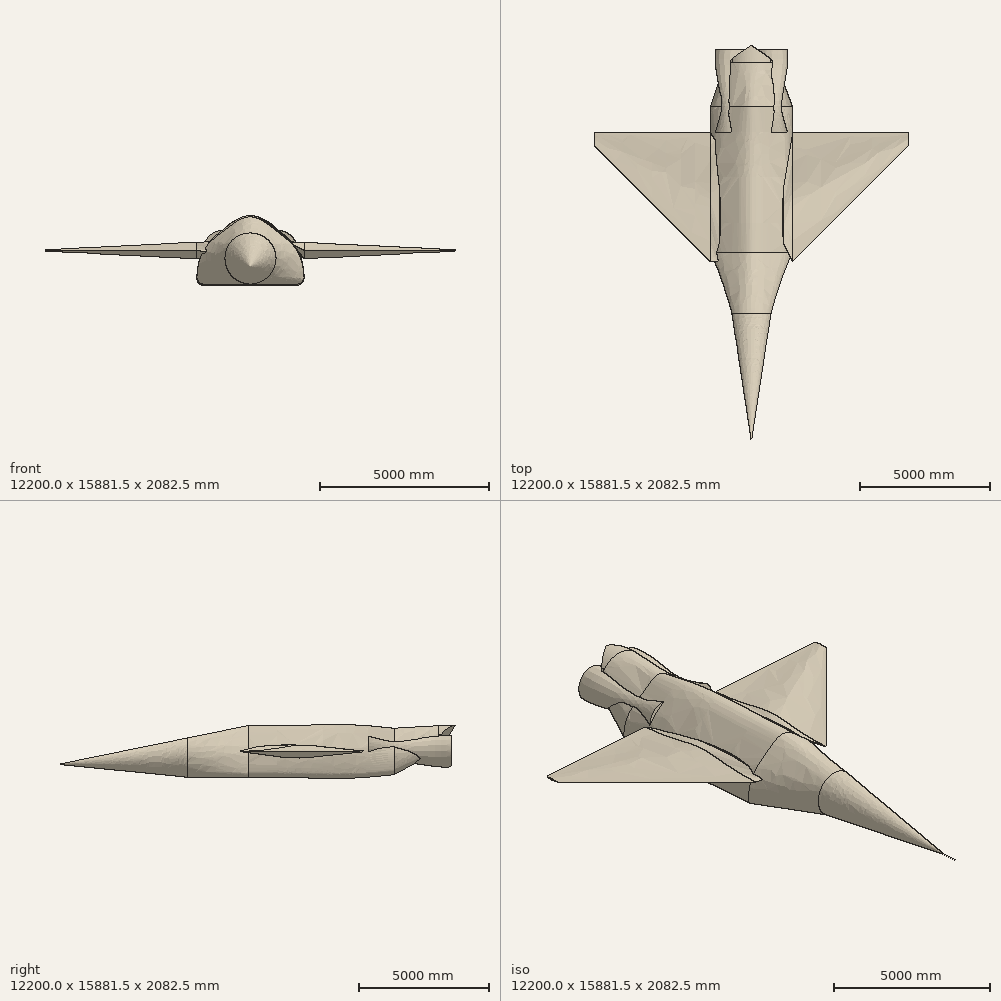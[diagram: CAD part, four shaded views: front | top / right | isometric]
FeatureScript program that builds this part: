
annotation { "Feature Type Name" : "Feature", "Feature Type Description" : "" }
export const myFeature = defineFeature(function(context is Context, id is Id, definition is map)
    precondition{}
    {
        {
            var Q0;
            Q0=qCreatedBy(makeId("Right.planeOp"),FACE);
            var sketch = newSketch(context, id + "F0", { "sketchPlane" : qUnion([Q0])});
            skLineSegment(sketch, "E0", {"start": v(0, 0) * mm, "end": v(-1750, 0) * mm});
            skLineSegment(sketch, "E1", {"start": v(-1750, 0) * mm, "end": v(-3500, 0) * mm});
            skLineSegment(sketch, "E2", {"start": v(-3500, 0) * mm, "end": v(-3500, -1000) * mm});
            skLineSegment(sketch, "E3", {"start": v(-3500, -1000) * mm, "end": v(-8500, -1000) * mm});
            skLineSegment(sketch, "E4", {"start": v(-8500, -1000) * mm, "end": v(-8500, -499.31) * mm});
            skLineSegment(sketch, "E5", {"start": v(-1151.4, 0) * mm, "end": v(-1151.4, 1000) * mm});
            skLineSegment(sketch, "E6", {"start": v(-1151.4, 1000) * mm, "end": v(-8500, -499.31) * mm});
            skLineSegment(sketch, "E7", {"start": v(-8500, -499.31) * mm, "end": v(-3500, -1000) * mm});
            skLineSegment(sketch, "E8", {"start": v(-3500, 0) * mm, "end": v(-3500, 520.82) * mm});
            skLineSegment(sketch, "E9", {"start": v(-8500, -499.31) * mm, "end": v(-8450, -499.31) * mm});
            skLineSegment(sketch, "E10", {"start": v(-8450, -499.31) * mm, "end": v(-8450, -489.1) * mm});
            skLineSegment(sketch, "E11", {"start": v(-8450, -499.31) * mm, "end": v(-8450, -504.32) * mm});
            skSolve(sketch);
        }
        {
            var Q0;
            Q0=sQuery(id+"F0.wireOp",EDGE,"E5");
            cPlane(context, id + "F1", {"entities" : qUnion([Q0]), "cplaneType" : CPlaneType.LINE_ANGLE, "offset" : 25 * mm, "angle" : 90 * degree, "oppositeDirection" : true, "width" : 150 * mm, "height" : 150 * mm});
        }
        {
            var Q0;
            Q0=qCreatedBy(id+"F1.planeOp",FACE);
            var sketch = newSketch(context, id + "F2", { "sketchPlane" : qUnion([Q0])});
            skLineSegment(sketch, "E12.top", {"start": v(-1394.2, -1000) * mm, "end": v(1394.2, -1000) * mm});
            skPoint(sketch, "E12.middle", {"position": v(0, 0) * mm});
            skFitSpline(sketch, "E13", {"points": [v(-1600, -1000) * mm, v(-848, 530) * mm, v(0, 1000) * mm, v(848, 530) * mm, v(1600, -1000) * mm], "startDerivative": vector(0, 10524.75) * mm, "endDerivative": vector(0, -10524.75) * mm});
            skArc(sketch, "E14", {"start": v(-735.27, 618.52) * mm, "mid": v(-1273.27, 435.52) * mm, "end": v(-1440.68, -107.53) * mm});
            skArc(sketch, "E15", {"start": v(1440.68, -107.53) * mm, "mid": v(1273.27, 435.52) * mm, "end": v(735.27, 618.52) * mm});
            skFitSpline(sketch, "E16.trimOffspring", {"points": [v(-1600, -1000) * mm, v(-848, 530) * mm, v(0, 1000) * mm, v(848, 530) * mm, v(1600, -1000) * mm], "startDerivative": vector(0, 10524.75) * mm, "endDerivative": vector(0, -10524.75) * mm});
            skFitSpline(sketch, "E17.trimOffspring", {"points": [v(-1600, -1000) * mm, v(-848, 530) * mm, v(0, 1000) * mm, v(848, 530) * mm, v(1600, -1000) * mm], "startDerivative": vector(0, 10524.75) * mm, "endDerivative": vector(0, -10524.75) * mm});
            skArc(sketch, "E18.filletArc", {"start": v(-1593.82, -787.83) * mm, "mid": v(-1539.85, -937.05) * mm, "end": v(-1394.2, -1000) * mm});
            skArc(sketch, "E19.filletArc", {"start": v(1394.2, -1000) * mm, "mid": v(1539.85, -937.05) * mm, "end": v(1593.82, -787.83) * mm});
            skSolve(sketch);
        }
        {
            var Q0;
            Q0=qCreatedBy(makeId("Front.planeOp"),FACE);
            var sketch = newSketch(context, id + "F3", { "sketchPlane" : qUnion([Q0])});
            skLineSegment(sketch, "E20.top", {"start": v(-1394.2, -1000) * mm, "end": v(1394.2, -1000) * mm});
            skPoint(sketch, "E20.middle", {"position": v(0, 0) * mm});
            skFitSpline(sketch, "E21", {"points": [v(-1600, -1000) * mm, v(-848, 530) * mm, v(0, 1000) * mm, v(848, 530) * mm, v(1600, -1000) * mm], "startDerivative": vector(0, 10524.75) * mm, "endDerivative": vector(0, -10524.75) * mm});
            skArc(sketch, "E22", {"start": v(-735.27, 618.52) * mm, "mid": v(-1273.27, 435.52) * mm, "end": v(-1440.68, -107.53) * mm});
            skArc(sketch, "E23", {"start": v(1440.68, -107.53) * mm, "mid": v(1273.27, 435.52) * mm, "end": v(735.27, 618.52) * mm});
            skFitSpline(sketch, "E24.trimOffspring", {"points": [v(-1600, -1000) * mm, v(-848, 530) * mm, v(0, 1000) * mm, v(848, 530) * mm, v(1600, -1000) * mm], "startDerivative": vector(0, 10524.75) * mm, "endDerivative": vector(0, -10524.75) * mm});
            skFitSpline(sketch, "E25.trimOffspring", {"points": [v(-1600, -1000) * mm, v(-848, 530) * mm, v(0, 1000) * mm, v(848, 530) * mm, v(1600, -1000) * mm], "startDerivative": vector(0, 10524.75) * mm, "endDerivative": vector(0, -10524.75) * mm});
            skArc(sketch, "E26.filletArc", {"start": v(-1593.82, -787.83) * mm, "mid": v(-1539.85, -937.05) * mm, "end": v(-1394.2, -1000) * mm});
            skArc(sketch, "E27.filletArc", {"start": v(1394.2, -1000) * mm, "mid": v(1539.85, -937.05) * mm, "end": v(1593.82, -787.83) * mm});
            skSolve(sketch);
        }
        {
            var Q0;
            Q0=qCreatedBy(makeId("Front.planeOp"),FACE);
            cPlane(context, id + "F4", {"entities" : qUnion([Q0]), "cplaneType" : CPlaneType.OFFSET, "offset" : 3500 * mm, "oppositeDirection" : true, "width" : 150 * mm, "height" : 150 * mm});
        }
        {
            var Q0;
            Q0=qCreatedBy(id+"F4.planeOp",FACE);
            var sketch = newSketch(context, id + "F5", { "sketchPlane" : qUnion([Q0])});
            skLineSegment(sketch, "E28.top", {"start": v(-1394.2, -1000) * mm, "end": v(1394.2, -1000) * mm});
            skPoint(sketch, "E28.middle", {"position": v(0, 0) * mm});
            skFitSpline(sketch, "E29", {"points": [v(-1600, -1000) * mm, v(-848, 530) * mm, v(0, 1000) * mm, v(848, 530) * mm, v(1600, -1000) * mm], "startDerivative": vector(0, 10524.75) * mm, "endDerivative": vector(0, -10524.75) * mm});
            skArc(sketch, "E30", {"start": v(-735.27, 618.52) * mm, "mid": v(-1273.27, 435.52) * mm, "end": v(-1440.68, -107.53) * mm});
            skArc(sketch, "E31", {"start": v(1440.68, -107.53) * mm, "mid": v(1273.27, 435.52) * mm, "end": v(735.27, 618.52) * mm});
            skFitSpline(sketch, "E32.trimOffspring", {"points": [v(-1600, -1000) * mm, v(-848, 530) * mm, v(0, 1000) * mm, v(848, 530) * mm, v(1600, -1000) * mm], "startDerivative": vector(0, 10524.75) * mm, "endDerivative": vector(0, -10524.75) * mm});
            skFitSpline(sketch, "E33.trimOffspring", {"points": [v(-1600, -1000) * mm, v(-848, 530) * mm, v(0, 1000) * mm, v(848, 530) * mm, v(1600, -1000) * mm], "startDerivative": vector(0, 10524.75) * mm, "endDerivative": vector(0, -10524.75) * mm});
            skArc(sketch, "E34.filletArc", {"start": v(-1593.82, -787.83) * mm, "mid": v(-1539.85, -937.05) * mm, "end": v(-1394.2, -1000) * mm});
            skArc(sketch, "E35.filletArc", {"start": v(1394.2, -1000) * mm, "mid": v(1539.85, -937.05) * mm, "end": v(1593.82, -787.83) * mm});
            skSolve(sketch);
        }
        {
            var Q0;
            Q0=qCreatedBy(makeId("Front.planeOp"),FACE);
            cPlane(context, id + "F6", {"entities" : qUnion([Q0]), "cplaneType" : CPlaneType.OFFSET, "offset" : 4500 * mm, "oppositeDirection" : true, "width" : 150 * mm, "height" : 150 * mm});
        }
        {
            var Q0;
            Q0=qCreatedBy(id+"F6.planeOp",FACE);
            var sketch = newSketch(context, id + "F7", { "sketchPlane" : qUnion([Q0])});
            skLineSegment(sketch, "E36.top", {"start": v(-1413.07, -900) * mm, "end": v(1413.07, -900) * mm});
            skPoint(sketch, "E36.middle", {"position": v(0, 0) * mm});
            skFitSpline(sketch, "E37", {"points": [v(-1600, -900) * mm, v(-784.42, 441.24) * mm, v(0, 900) * mm, v(784.42, 441.24) * mm, v(1600, -900) * mm], "startDerivative": vector(0, 9508.62) * mm, "endDerivative": vector(0, -9508.62) * mm});
            skArc(sketch, "E38", {"start": v(-719.25, 488.69) * mm, "mid": v(-1131.76, 394.84) * mm, "end": v(-1324.66, 18.33) * mm});
            skArc(sketch, "E39", {"start": v(1324.66, 18.33) * mm, "mid": v(1131.76, 394.84) * mm, "end": v(719.25, 488.69) * mm});
            skFitSpline(sketch, "E40.trimOffspring", {"points": [v(-1600, -900) * mm, v(-784.42, 441.24) * mm, v(0, 900) * mm, v(784.42, 441.24) * mm, v(1600, -900) * mm], "startDerivative": vector(0, 9508.62) * mm, "endDerivative": vector(0, -9508.62) * mm});
            skFitSpline(sketch, "E41.trimOffspring", {"points": [v(-1600, -900) * mm, v(-784.42, 441.24) * mm, v(0, 900) * mm, v(784.42, 441.24) * mm, v(1600, -900) * mm], "startDerivative": vector(0, 9508.62) * mm, "endDerivative": vector(0, -9508.62) * mm});
            skArc(sketch, "E42.filletArc", {"start": v(-1592.48, -705.43) * mm, "mid": v(-1545.4, -842.02) * mm, "end": v(-1413.07, -900) * mm});
            skArc(sketch, "E43.filletArc", {"start": v(1413.07, -900) * mm, "mid": v(1545.4, -842.02) * mm, "end": v(1592.48, -705.43) * mm});
            skLineSegment(sketch, "E44", {"start": v(-719.25, 488.69) * mm, "end": v(-1324.66, 18.33) * mm, "construction": true});
            skLineSegment(sketch, "E45", {"start": v(719.25, 488.69) * mm, "end": v(1324.66, 18.33) * mm, "construction": true});
            skSolve(sketch);
        }
        {
            var Q0;
            Q0=qCreatedBy(makeId("Front.planeOp"),FACE);
            cPlane(context, id + "F8", {"entities" : qUnion([Q0]), "cplaneType" : CPlaneType.OFFSET, "offset" : 6232.05 * mm, "oppositeDirection" : true, "width" : 150 * mm, "height" : 150 * mm});
        }
        {
            var Q0;
            Q0=qCreatedBy(id+"F8.planeOp",FACE);
            var sketch = newSketch(context, id + "F9", { "sketchPlane" : qUnion([Q0])});
            skArc(sketch, "E46", {"start": v(998.61, 52.63) * mm, "mid": v(0, 1000) * mm, "end": v(-998.61, 52.63) * mm});
            skLineSegment(sketch, "E47", {"start": v(0, 0) * mm, "end": v(-948.68, 0) * mm});
            skLineSegment(sketch, "E48", {"start": v(0, 0) * mm, "end": v(948.68, 0) * mm});
            skLineSegment(sketch, "E49", {"start": v(0, 1000) * mm, "end": v(0, 675) * mm, "construction": true});
            skLineSegment(sketch, "E50", {"start": v(0, 675) * mm, "end": v(-737.82, 675) * mm, "construction": true});
            skLineSegment(sketch, "E51", {"start": v(0, 675) * mm, "end": v(737.82, 675) * mm, "construction": true});
            skPoint(sketch, "E52.visualSharp", {"position": v(-1000, 0) * mm});
            skArc(sketch, "E52.filletArc", {"start": v(-998.61, 52.63) * mm, "mid": v(-984.96, 15.59) * mm, "end": v(-948.68, 0) * mm});
            skPoint(sketch, "E53.visualSharp", {"position": v(1000, 0) * mm});
            skArc(sketch, "E53.filletArc", {"start": v(948.68, 0) * mm, "mid": v(984.96, 15.59) * mm, "end": v(998.61, 52.63) * mm});
            skSolve(sketch);
        }
        {
            var Q0;
            Q0=makeQuery(id+"F2.imprint","IMPRINT",FACE,{"disambiguationData":[TD([[makeQuery(id+"F2.imprint","IMPRINT",EDGE,{"derivedFrom":sQuery(id+"F2.wireOp",EDGE,"E12.top")}),1.0]])]});
            var Q1;
            Q1=makeQuery(id+"F3.imprint","IMPRINT",FACE,{"disambiguationData":[TD([[makeQuery(id+"F3.imprint","IMPRINT",EDGE,{"derivedFrom":sQuery(id+"F3.wireOp",EDGE,"E20.top")}),1.0]])]});
            var Q2;
            Q2=makeQuery(id+"F5.imprint","IMPRINT",FACE,{"disambiguationData":[TD([[makeQuery(id+"F5.imprint","IMPRINT",EDGE,{"derivedFrom":sQuery(id+"F5.wireOp",EDGE,"E28.top")}),1.0]])]});
            var Q3;
            Q3=makeQuery(id+"F7.imprint","IMPRINT",FACE,{"disambiguationData":[TD([[makeQuery(id+"F7.imprint","IMPRINT",EDGE,{"derivedFrom":sQuery(id+"F7.wireOp",EDGE,"E36.top")}),1.0]])]});
            loft(context, id + "F10", {"sheetProfilesArray" : [{ "sheetProfileEntities" : qUnion([Q0]) }, { "sheetProfileEntities" : qUnion([Q1]) }, { "sheetProfileEntities" : qUnion([Q2]) }, { "sheetProfileEntities" : qUnion([Q3]) }]});
        }
        {
            var Q0;
            Q0=sQuery(id+"F7.wireOp",EDGE,"E44");
            var Q1;
            Q1=sQuery(id+"F9.wireOp",VERTEX,"E50.end");
            cPlane(context, id + "F11", {"entities" : qUnion([Q0, Q1]), "cplaneType" : CPlaneType.LINE_ANGLE, "offset" : 25 * mm, "angle" : 180 * degree, "width" : 150 * mm, "height" : 150 * mm});
        }
        {
            var Q0;
            Q0=qCreatedBy(id+"F11.planeOp",FACE);
            var sketch = newSketch(context, id + "F12", { "sketchPlane" : qUnion([Q0])});
            skLineSegment(sketch, "E54", {"start": v(-589.34, 4526.34) * mm, "end": v(-612.8, 6268.32) * mm});
            skLineSegment(sketch, "E55", {"start": v(-1354.08, 4472.19) * mm, "end": v(-612.8, 6268.32) * mm});
            skSolve(sketch);
        }
        {
            var Q0;
            Q0=sQuery(id+"F7.wireOp",EDGE,"E45");
            var Q1;
            Q1=sQuery(id+"F9.wireOp",VERTEX,"E51.end");
            cPlane(context, id + "F13", {"entities" : qUnion([Q0, Q1]), "cplaneType" : CPlaneType.LINE_ANGLE, "offset" : 25 * mm, "angle" : 0 * degree, "width" : 150 * mm, "height" : 150 * mm});
        }
        {
            var Q0;
            Q0=qCreatedBy(id+"F13.planeOp",FACE);
            var sketch = newSketch(context, id + "F14", { "sketchPlane" : qUnion([Q0])});
            skLineSegment(sketch, "E56", {"start": v(589.34, 4526.34) * mm, "end": v(612.8, 6268.32) * mm});
            skLineSegment(sketch, "E57", {"start": v(1354.08, 4472.19) * mm, "end": v(612.8, 6268.32) * mm});
            skSolve(sketch);
        }
        {
            var Q1;
            Q1=makeQuery(id+"F10.opLoft","CAP_FACE",FACE,{"disambiguationData":[OSD([makeQuery(id+"F7.imprint","IMPRINT",FACE,{"disambiguationData":[TD([[makeQuery(id+"F7.imprint","IMPRINT",EDGE,{"derivedFrom":sQuery(id+"F7.wireOp",EDGE,"E36.top")}),1.0]])]})])],"isStart":true});
            var Q2;
            Q2=makeQuery(id+"F9.imprint","IMPRINT",FACE,{"disambiguationData":[TD([[makeQuery(id+"F9.imprint","IMPRINT",EDGE,{"derivedFrom":sQuery(id+"F9.wireOp",EDGE,"E46")}),1.0]])]});
            var Q3;
            Q3=sQuery(id+"F12.wireOp",EDGE,"E54");
            var Q4;
            Q4=sQuery(id+"F14.wireOp",EDGE,"E56");
            loft(context, id + "F15", {"operationType" : NewBodyOperationType.ADD, "addGuides" : true, "sheetProfilesArray" : [{ "sheetProfileEntities" : qUnion([Q1]) }, { "sheetProfileEntities" : qUnion([Q2]) }], "guidesArray" : [{ "guideEntities" : qUnion([Q3]), "guideDerivativeType" : LoftGuideDerivativeType.DEFAULT, "guideDerivativeMagnitude" : 1 }, { "guideEntities" : qUnion([Q4]), "guideDerivativeType" : LoftGuideDerivativeType.DEFAULT, "guideDerivativeMagnitude" : 1 }]});
        }
        {
            var Q0;
            Q0=makeQuery(id+"F15.opLoft","CAP_FACE",FACE,{"disambiguationData":[OSD([makeQuery(id+"F9.imprint","IMPRINT",FACE,{"disambiguationData":[TD([[makeQuery(id+"F9.imprint","IMPRINT",EDGE,{"derivedFrom":sQuery(id+"F9.wireOp",EDGE,"E46")}),1.0]])]})])],"isStart":true});
            extrude(context, id + "F16", {"entities" : qUnion([Q0]), "operationType" : NewBodyOperationType.ADD, "depth" : 649.4 * mm, "offsetDistance" : 25 * mm});
        }
        {
            var Q0;
            Q0=qCreatedBy(makeId("Right.planeOp"),FACE);
            var sketch = newSketch(context, id + "F17", { "sketchPlane" : qUnion([Q0])});
            skLineSegment(sketch, "E58", {"start": v(0, 0) * mm, "end": v(4500, 0) * mm});
            skLineSegment(sketch, "E59", {"start": v(4500, 0) * mm, "end": v(6232.05, 0) * mm});
            skLineSegment(sketch, "E60", {"start": v(4500, 0) * mm, "end": v(4500, 1000) * mm});
            skLineSegment(sketch, "E61", {"start": v(4500, 1000) * mm, "end": v(6881.46, 1000) * mm});
            skLineSegment(sketch, "E62", {"start": v(6881.46, 1000) * mm, "end": v(6881.46, -1000) * mm});
            skLineSegment(sketch, "E63", {"start": v(6881.46, 1000) * mm, "end": v(6232.05, 0) * mm});
            skLineSegment(sketch, "E64", {"start": v(6232.05, 0) * mm, "end": v(5582.64, -1000) * mm});
            skLineSegment(sketch, "E65", {"start": v(5582.64, -1000) * mm, "end": v(6881.46, -1000) * mm});
            skSolve(sketch);
        }
        {
            var Q0;
            Q0=makeQuery(id+"F17.imprint","IMPRINT",FACE,{"disambiguationData":[TD([[makeQuery(id+"F17.imprint","IMPRINT",EDGE,{"derivedFrom":sQuery(id+"F17.wireOp",EDGE,"E62")}),-1.0]])]});
            var Q1;
            Q1=sQuery(id+"F17.wireOp",EDGE,"E61");
            revolve(context, id + "F18", {"operationType" : NewBodyOperationType.REMOVE, "entities" : qUnion([Q0]), "axis" : qUnion([Q1]), "revolveType" : RevolveType.SYMMETRIC, "oppositeDirection" : true, "angle" : 182 * degree});
        }
        {
            var Q0;
            Q0=qCreatedBy(id+"F1.planeOp",FACE);
            var sketch = newSketch(context, id + "F19", { "sketchPlane" : qUnion([Q0])});
            skLineSegment(sketch, "E66.top", {"start": v(-1394.2, -1000) * mm, "end": v(1394.2, -1000) * mm});
            skPoint(sketch, "E66.middle", {"position": v(0, 0) * mm});
            skFitSpline(sketch, "E67", {"points": [v(-1600, -1000) * mm, v(-848, 530) * mm, v(0, 1000) * mm, v(848, 530) * mm, v(1600, -1000) * mm], "startDerivative": vector(0, 10524.75) * mm, "endDerivative": vector(0, -10524.75) * mm});
            skArc(sketch, "E68.filletArc", {"start": v(-1593.82, -787.83) * mm, "mid": v(-1539.85, -937.05) * mm, "end": v(-1394.2, -1000) * mm});
            skArc(sketch, "E69.filletArc", {"start": v(1394.2, -1000) * mm, "mid": v(1539.85, -937.05) * mm, "end": v(1593.82, -787.83) * mm});
            skLineSegment(sketch, "E70", {"start": v(-1593.82, -787.83) * mm, "end": v(-1394.2, -1000) * mm, "construction": true});
            skLineSegment(sketch, "E71", {"start": v(1593.82, -787.83) * mm, "end": v(1394.2, -1000) * mm, "construction": true});
            skSolve(sketch);
        }
        {
            var Q0;
            Q0=qCreatedBy(makeId("Front.planeOp"),FACE);
            cPlane(context, id + "F20", {"entities" : qUnion([Q0]), "cplaneType" : CPlaneType.OFFSET, "offset" : 3500 * mm, "width" : 150 * mm, "height" : 150 * mm});
        }
        {
            var Q0;
            Q0=qCreatedBy(id+"F20.planeOp",FACE);
            var sketch = newSketch(context, id + "F21", { "sketchPlane" : qUnion([Q0])});
            skCircle(sketch, "E72", {"center": v(0, -239.59) * mm, "radius": 760.41 * mm});
            skLineSegment(sketch, "E73", {"start": v(0, -1000) * mm, "end": v(0, -800) * mm, "construction": true});
            skLineSegment(sketch, "E74", {"start": v(0, -800) * mm, "end": v(-513.97, -800) * mm, "construction": true});
            skLineSegment(sketch, "E75", {"start": v(0, -800) * mm, "end": v(513.97, -800) * mm, "construction": true});
            skSolve(sketch);
        }
        {
            var Q0;
            Q0=qCreatedBy(makeId("Front.planeOp"),FACE);
            cPlane(context, id + "F22", {"entities" : qUnion([Q0]), "cplaneType" : CPlaneType.OFFSET, "offset" : 8450 * mm, "width" : 150 * mm, "height" : 150 * mm});
        }
        {
            var Q0;
            Q0=qCreatedBy(id+"F22.planeOp",FACE);
            var sketch = newSketch(context, id + "F23", { "sketchPlane" : qUnion([Q0])});
            skCircle(sketch, "E76", {"center": v(0, -496.71) * mm, "radius": 7.6 * mm});
            skSolve(sketch);
        }
        {
            var Q0;
            Q0=sQuery(id+"F19.wireOp",EDGE,"E70");
            var Q1;
            Q1=sQuery(id+"F21.wireOp",VERTEX,"E74.end");
            cPlane(context, id + "F24", {"entities" : qUnion([Q0, Q1]), "cplaneType" : CPlaneType.LINE_ANGLE, "offset" : 25 * mm, "angle" : 0 * degree, "width" : 150 * mm, "height" : 150 * mm});
        }
        {
            var Q0;
            Q0=qCreatedBy(id+"F24.planeOp",FACE);
            var sketch = newSketch(context, id + "F25", { "sketchPlane" : qUnion([Q0])});
            skLineSegment(sketch, "E77", {"start": v(3032.27, -230.44) * mm, "end": v(558.11, 518.4) * mm});
            skLineSegment(sketch, "E78", {"start": v(3032.27, -230.44) * mm, "end": v(558.11, 227.09) * mm});
            skSolve(sketch);
        }
        {
            var Q0;
            Q0=sQuery(id+"F19.wireOp",EDGE,"E71");
            var Q1;
            Q1=sQuery(id+"F21.wireOp",VERTEX,"E75.end");
            cPlane(context, id + "F26", {"entities" : qUnion([Q0, Q1]), "cplaneType" : CPlaneType.LINE_ANGLE, "offset" : 25 * mm, "angle" : 180 * degree, "width" : 150 * mm, "height" : 150 * mm});
        }
        {
            var Q0;
            Q0=qCreatedBy(id+"F26.planeOp",FACE);
            var sketch = newSketch(context, id + "F27", { "sketchPlane" : qUnion([Q0])});
            skLineSegment(sketch, "E79", {"start": v(-3032.27, -230.44) * mm, "end": v(-558.11, 518.4) * mm});
            skLineSegment(sketch, "E80", {"start": v(-3032.27, -230.44) * mm, "end": v(-558.11, 227.09) * mm});
            skSolve(sketch);
        }
        {
            var Q1;
            Q1=makeQuery(id+"F19.imprint","IMPRINT",FACE,{"disambiguationData":[TD([[makeQuery(id+"F19.imprint","IMPRINT",EDGE,{"derivedFrom":sQuery(id+"F19.wireOp",EDGE,"E66.top")}),1.0]])]});
            var Q2;
            Q2=makeQuery(id+"F21.imprint","IMPRINT",FACE,{"disambiguationData":[TD([[makeQuery(id+"F21.imprint","IMPRINT",EDGE,{"derivedFrom":sQuery(id+"F21.wireOp",EDGE,"E72")}),1.0]])]});
            var Q3;
            Q3=sQuery(id+"F25.wireOp",EDGE,"E77");
            var Q4;
            Q4=sQuery(id+"F27.wireOp",EDGE,"E79");
            loft(context, id + "F28", {"operationType" : NewBodyOperationType.ADD, "addGuides" : true, "sheetProfilesArray" : [{ "sheetProfileEntities" : qUnion([Q1]) }, { "sheetProfileEntities" : qUnion([Q2]) }], "guidesArray" : [{ "guideEntities" : qUnion([Q3]), "guideDerivativeType" : LoftGuideDerivativeType.DEFAULT, "guideDerivativeMagnitude" : 1 }, { "guideEntities" : qUnion([Q4]), "guideDerivativeType" : LoftGuideDerivativeType.DEFAULT, "guideDerivativeMagnitude" : 1 }]});
        }
        {
            var Q1;
            Q1=makeQuery(id+"F28.opLoft","CAP_FACE",FACE,{"disambiguationData":[OSD([makeQuery(id+"F21.imprint","IMPRINT",FACE,{"disambiguationData":[TD([[makeQuery(id+"F21.imprint","IMPRINT",EDGE,{"derivedFrom":sQuery(id+"F21.wireOp",EDGE,"E72")}),1.0]])]})])],"isStart":true});
            var Q2;
            Q2=makeQuery(id+"F23.imprint","IMPRINT",FACE,{"disambiguationData":[TD([[makeQuery(id+"F23.imprint","IMPRINT",EDGE,{"derivedFrom":sQuery(id+"F23.wireOp",EDGE,"E76")}),1.0]])]});
            loft(context, id + "F29", {"operationType" : NewBodyOperationType.ADD, "sheetProfilesArray" : [{ "sheetProfileEntities" : qUnion([Q1]) }, { "sheetProfileEntities" : qUnion([Q2]) }]});
        }
        {
            var Q0;
            Q0=makeQuery(id+"F29.opLoft","CAP_FACE",FACE,{"disambiguationData":[OSD([makeQuery(id+"F23.imprint","IMPRINT",FACE,{"disambiguationData":[TD([[makeQuery(id+"F23.imprint","IMPRINT",EDGE,{"derivedFrom":sQuery(id+"F23.wireOp",EDGE,"E76")}),1.0]])]})])],"isStart":true});
            extrude(context, id + "F30", {"entities" : qUnion([Q0]), "operationType" : NewBodyOperationType.ADD, "depth" : 550 * mm, "offsetDistance" : 25 * mm});
        }
        {
            var Q0;
            Q0=qCreatedBy(makeId("Front.planeOp"),FACE);
            cPlane(context, id + "F31", {"entities" : qUnion([Q0]), "cplaneType" : CPlaneType.OFFSET, "offset" : 3500 * mm, "oppositeDirection" : true, "width" : 150 * mm, "height" : 150 * mm});
        }
        {
            var Q0;
            Q0=qCreatedBy(id+"F31.planeOp",FACE);
            var sketch = newSketch(context, id + "F32", { "sketchPlane" : qUnion([Q0])});
            skCircle(sketch, "E81", {"center": v(-800, 0) * mm, "radius": 600 * mm});
            skCircle(sketch, "E82", {"center": v(800, 0) * mm, "radius": 600 * mm});
            skSolve(sketch);
        }
        {
            var Q0;
            Q0=qCreatedBy(makeId("Front.planeOp"),FACE);
            cPlane(context, id + "F33", {"entities" : qUnion([Q0]), "cplaneType" : CPlaneType.OFFSET, "offset" : 4500 * mm, "oppositeDirection" : true, "width" : 150 * mm, "height" : 150 * mm});
        }
        {
            var Q0;
            Q0=qCreatedBy(id+"F33.planeOp",FACE);
            var sketch = newSketch(context, id + "F34", { "sketchPlane" : qUnion([Q0])});
            skCircle(sketch, "E83", {"center": v(-800, 0) * mm, "radius": 400 * mm});
            skCircle(sketch, "E84", {"center": v(800, 0) * mm, "radius": 400 * mm});
            skSolve(sketch);
        }
        {
            var Q0;
            Q0=qCreatedBy(makeId("Front.planeOp"),FACE);
            cPlane(context, id + "F35", {"entities" : qUnion([Q0]), "cplaneType" : CPlaneType.OFFSET, "offset" : 6232.05 * mm, "oppositeDirection" : true, "width" : 150 * mm, "height" : 150 * mm});
        }
        {
            var Q0;
            Q0=qCreatedBy(id+"F35.planeOp",FACE);
            var sketch = newSketch(context, id + "F36", { "sketchPlane" : qUnion([Q0])});
            skCircle(sketch, "E85", {"center": v(-800, 0) * mm, "radius": 600 * mm});
            skCircle(sketch, "E86", {"center": v(800, 0) * mm, "radius": 600 * mm});
            skSolve(sketch);
        }
        {
            var Q0;
            Q0=qCreatedBy(makeId("Front.planeOp"),FACE);
            cPlane(context, id + "F37", {"entities" : qUnion([Q0]), "cplaneType" : CPlaneType.OFFSET, "offset" : 6732.05 * mm, "oppositeDirection" : true, "width" : 150 * mm, "height" : 150 * mm});
        }
        {
            var Q0;
            Q0=qCreatedBy(id+"F37.planeOp",FACE);
            var sketch = newSketch(context, id + "F38", { "sketchPlane" : qUnion([Q0])});
            skCircle(sketch, "E87", {"center": v(-800, 0) * mm, "radius": 600 * mm});
            skCircle(sketch, "E88", {"center": v(800, 0) * mm, "radius": 600 * mm});
            skSolve(sketch);
        }
        {
            var Q0;
            Q0=makeQuery(id+"F32.imprint","IMPRINT",FACE,{"disambiguationData":[TD([[makeQuery(id+"F32.imprint","IMPRINT",EDGE,{"derivedFrom":sQuery(id+"F32.wireOp",EDGE,"E81")}),1.0]])]});
            var Q1;
            Q1=makeQuery(id+"F34.imprint","IMPRINT",FACE,{"disambiguationData":[TD([[makeQuery(id+"F34.imprint","IMPRINT",EDGE,{"derivedFrom":sQuery(id+"F34.wireOp",EDGE,"E83")}),1.0]])]});
            var Q2;
            Q2=makeQuery(id+"F36.imprint","IMPRINT",FACE,{"disambiguationData":[TD([[makeQuery(id+"F36.imprint","IMPRINT",EDGE,{"derivedFrom":sQuery(id+"F36.wireOp",EDGE,"E85")}),1.0]])]});
            var Q3;
            Q3=makeQuery(id+"F38.imprint","IMPRINT",FACE,{"disambiguationData":[TD([[makeQuery(id+"F38.imprint","IMPRINT",EDGE,{"derivedFrom":sQuery(id+"F38.wireOp",EDGE,"E87")}),1.0]])]});
            loft(context, id + "F39", {"sheetProfilesArray" : [{ "sheetProfileEntities" : qUnion([Q0]) }, { "sheetProfileEntities" : qUnion([Q1]) }, { "sheetProfileEntities" : qUnion([Q2]) }, { "sheetProfileEntities" : qUnion([Q3]) }]});
        }
        {
            var Q0;
            Q0=makeQuery(id+"F32.imprint","IMPRINT",FACE,{"disambiguationData":[TD([[makeQuery(id+"F32.imprint","IMPRINT",EDGE,{"derivedFrom":sQuery(id+"F32.wireOp",EDGE,"E82")}),1.0]])]});
            var Q1;
            Q1=makeQuery(id+"F34.imprint","IMPRINT",FACE,{"disambiguationData":[TD([[makeQuery(id+"F34.imprint","IMPRINT",EDGE,{"derivedFrom":sQuery(id+"F34.wireOp",EDGE,"E84")}),1.0]])]});
            var Q2;
            Q2=makeQuery(id+"F36.imprint","IMPRINT",FACE,{"disambiguationData":[TD([[makeQuery(id+"F36.imprint","IMPRINT",EDGE,{"derivedFrom":sQuery(id+"F36.wireOp",EDGE,"E86")}),1.0]])]});
            var Q3;
            Q3=makeQuery(id+"F38.imprint","IMPRINT",FACE,{"disambiguationData":[TD([[makeQuery(id+"F38.imprint","IMPRINT",EDGE,{"derivedFrom":sQuery(id+"F38.wireOp",EDGE,"E88")}),1.0]])]});
            loft(context, id + "F40", {"sheetProfilesArray" : [{ "sheetProfileEntities" : qUnion([Q0]) }, { "sheetProfileEntities" : qUnion([Q1]) }, { "sheetProfileEntities" : qUnion([Q2]) }, { "sheetProfileEntities" : qUnion([Q3]) }]});
        }
        {
            var Q0;
            Q0=qCreatedBy(makeId("Right.planeOp"),FACE);
            var sketch = newSketch(context, id + "F41", { "sketchPlane" : qUnion([Q0])});
            skFitSpline(sketch, "E89", {"points": [v(-1500, -50) * mm, v(0, 250) * mm, v(3000, -50) * mm, v(0, -250) * mm, v(-1500, -50) * mm]});
            skSolve(sketch);
        }
        {
            var Q0;
            Q0=qCreatedBy(makeId("Right.planeOp"),FACE);
            cPlane(context, id + "F42", {"entities" : qUnion([Q0]), "cplaneType" : CPlaneType.OFFSET, "offset" : 1600 * mm, "oppositeDirection" : true, "width" : 150 * mm, "height" : 150 * mm});
        }
        {
            var Q0;
            Q0=qCreatedBy(id+"F42.planeOp",FACE);
            var sketch = newSketch(context, id + "F43", { "sketchPlane" : qUnion([Q0])});
            skFitSpline(sketch, "E90", {"points": [v(-1500, 0) * mm, v(1000, 250) * mm, v(3500, 0) * mm], "startDerivative": vector(7500, 0) * mm, "endDerivative": vector(7500, 0) * mm});
            skFitSpline(sketch, "E91", {"points": [v(-1500, 0) * mm, v(1000, -250) * mm, v(3500, 0) * mm], "startDerivative": vector(5000, -750) * mm, "endDerivative": vector(7500, 0) * mm});
            skSolve(sketch);
        }
        {
            var Q0;
            Q0=qCreatedBy(makeId("Right.planeOp"),FACE);
            cPlane(context, id + "F44", {"entities" : qUnion([Q0]), "cplaneType" : CPlaneType.OFFSET, "offset" : 1600 * mm, "width" : 150 * mm, "height" : 150 * mm});
        }
        {
            var Q0;
            Q0=qCreatedBy(id+"F44.planeOp",FACE);
            var sketch = newSketch(context, id + "F45", { "sketchPlane" : qUnion([Q0])});
            skFitSpline(sketch, "E92", {"points": [v(-1500, 0) * mm, v(1000, 250) * mm, v(3500, 0) * mm], "startDerivative": vector(7500, 0) * mm, "endDerivative": vector(7500, 0) * mm});
            skFitSpline(sketch, "E93", {"points": [v(-1500, 0) * mm, v(1000, -250) * mm, v(3500, 0) * mm], "startDerivative": vector(5000, -750) * mm, "endDerivative": vector(7500, 0) * mm});
            skSolve(sketch);
        }
        {
            var Q0;
            Q0=qCreatedBy(makeId("Right.planeOp"),FACE);
            cPlane(context, id + "F46", {"entities" : qUnion([Q0]), "cplaneType" : CPlaneType.OFFSET, "offset" : 6100 * mm, "oppositeDirection" : true, "width" : 150 * mm, "height" : 150 * mm});
        }
        {
            var Q0;
            Q0=qCreatedBy(id+"F46.planeOp",FACE);
            var sketch = newSketch(context, id + "F47", { "sketchPlane" : qUnion([Q0])});
            skFitSpline(sketch, "E94", {"points": [v(3000, 0) * mm, v(3250, 25) * mm, v(3500, 0) * mm], "startDerivative": vector(750, 0) * mm, "endDerivative": vector(750, 0) * mm});
            skFitSpline(sketch, "E95", {"points": [v(3000, 0) * mm, v(3250, -25) * mm, v(3500, 0) * mm], "startDerivative": vector(500, -75) * mm, "endDerivative": vector(750, 0) * mm});
            skSolve(sketch);
        }
        {
            var Q0;
            Q0=qCreatedBy(makeId("Right.planeOp"),FACE);
            cPlane(context, id + "F48", {"entities" : qUnion([Q0]), "cplaneType" : CPlaneType.OFFSET, "offset" : 6100 * mm, "width" : 150 * mm, "height" : 150 * mm});
        }
        {
            var Q0;
            Q0=qCreatedBy(id+"F48.planeOp",FACE);
            var sketch = newSketch(context, id + "F49", { "sketchPlane" : qUnion([Q0])});
            skFitSpline(sketch, "E96", {"points": [v(3000, 0) * mm, v(3250, 25) * mm, v(3500, 0) * mm], "startDerivative": vector(750, 0) * mm, "endDerivative": vector(750, 0) * mm});
            skFitSpline(sketch, "E97", {"points": [v(3000, 0) * mm, v(3250, -25) * mm, v(3500, 0) * mm], "startDerivative": vector(500, -75) * mm, "endDerivative": vector(750, 0) * mm});
            skSolve(sketch);
        }
        {
            var Q0;
            Q0 = qSketchRegion(id + "F41", true);
            extrude(context, id + "F50", {"entities" : qUnion([Q0]), "endBound" : BoundingType.SYMMETRIC, "depth" : 2500 * mm, "offsetDistance" : 25 * mm});
        }
        {
            var Q1;
            Q1=makeQuery(id+"F50.opExtrude","CAP_FACE",FACE,{"disambiguationData":[OSD([sQuery(id+"F41.wireOp",EDGE,"E89")])],"isStart":true});
            var Q2;
            {var subQ0=sQuery(id+"F43.wireOp",EDGE,"E90");Q2=makeQuery(id+"F43.imprint","IMPRINT",FACE,{"disambiguationData":[TD([[makeQuery(id+"F43.imprint","IMPRINT",EDGE,{"derivedFrom":subQ0}),-1.0]])]});}
            loft(context, id + "F51", {"operationType" : NewBodyOperationType.ADD, "sheetProfilesArray" : [{ "sheetProfileEntities" : qUnion([Q1]) }, { "sheetProfileEntities" : qUnion([Q2]) }]});
        }
        {
            var Q1;
            Q1=makeQuery(id+"F50.opExtrude","CAP_FACE",FACE,{"disambiguationData":[OSD([sQuery(id+"F41.wireOp",EDGE,"E89")])],"isStart":false});
            var Q2;
            {var subQ0=sQuery(id+"F45.wireOp",EDGE,"E92");Q2=makeQuery(id+"F45.imprint","IMPRINT",FACE,{"disambiguationData":[TD([[makeQuery(id+"F45.imprint","IMPRINT",EDGE,{"derivedFrom":subQ0}),-1.0]])]});}
            loft(context, id + "F52", {"operationType" : NewBodyOperationType.ADD, "sheetProfilesArray" : [{ "sheetProfileEntities" : qUnion([Q1]) }, { "sheetProfileEntities" : qUnion([Q2]) }]});
        }
        {
            var Q1;
            {var subQ0=sQuery(id+"F43.wireOp",EDGE,"E90");Q1=makeQuery(id+"F51.opLoft","CAP_FACE",FACE,{"disambiguationData":[OSD([makeQuery(id+"F43.imprint","IMPRINT",FACE,{"disambiguationData":[TD([[makeQuery(id+"F43.imprint","IMPRINT",EDGE,{"derivedFrom":subQ0}),-1.0]])]})])],"isStart":true});}
            var Q2;
            {var subQ0=sQuery(id+"F47.wireOp",EDGE,"E94");Q2=makeQuery(id+"F47.imprint","IMPRINT",FACE,{"disambiguationData":[TD([[makeQuery(id+"F47.imprint","IMPRINT",EDGE,{"derivedFrom":subQ0}),-1.0]])]});}
            loft(context, id + "F53", {"operationType" : NewBodyOperationType.ADD, "sheetProfilesArray" : [{ "sheetProfileEntities" : qUnion([Q1]) }, { "sheetProfileEntities" : qUnion([Q2]) }]});
        }
        {
            var Q1;
            {var subQ0=sQuery(id+"F45.wireOp",EDGE,"E92");Q1=makeQuery(id+"F52.opLoft","CAP_FACE",FACE,{"disambiguationData":[OSD([makeQuery(id+"F45.imprint","IMPRINT",FACE,{"disambiguationData":[TD([[makeQuery(id+"F45.imprint","IMPRINT",EDGE,{"derivedFrom":subQ0}),-1.0]])]})])],"isStart":true});}
            var Q2;
            {var subQ0=sQuery(id+"F49.wireOp",EDGE,"E96");Q2=makeQuery(id+"F49.imprint","IMPRINT",FACE,{"disambiguationData":[TD([[makeQuery(id+"F49.imprint","IMPRINT",EDGE,{"derivedFrom":subQ0}),-1.0]])]});}
            loft(context, id + "F54", {"operationType" : NewBodyOperationType.ADD, "sheetProfilesArray" : [{ "sheetProfileEntities" : qUnion([Q1]) }, { "sheetProfileEntities" : qUnion([Q2]) }]});
        }
    });
